# Revit family: vanity unit-hansgrohe-54195XXX-Xevolos E Vanity unit Slate Matt Grey 1180_550 with 2 drawers for consoles with countertop basin ground
name_source: partatom
category: Furniture
units: mm (PartAtom-declared; Revit-internal decimal feet)

## family parameters
Always vertical = Yes
Cut with Voids When Loaded = No
OmniClass Number = 23.40.00.00
OmniClass Title = Equipment and Furnishings
Room Calculation Point = No
Shared = Yes
Work Plane-Based = No

## types (6) — shared parameters
BASENUMBER = 54195
BIMOBJECT = Sanitary: Compound units
CATALOG = Hansgrohe
COLLECTION = vanity unit
COLLECTIONSET = Xevolos E
DESIGN = Germany
ETIM = EC011381 | Bathroom furniture set
IFC = Furnishing element
L = 1180
MASTERFORMAT = 12 35 30.23 | Bathroom Casework
Manufacturer = Hansgrohe
NAME = Xevolos E Vanity unit Slate Matt Grey 1180/550 with 2 drawers for consoles with countertop basin ground
NBSYN = $ARTNR.-$OBERFLAECHE.-$SURFACE.-$LODLEVEL.
NN = Vanity unit with 2 drawers for consoles with countertop basin ground
OBERFLAECHE = SLATE_MATT_GREY
OBJECTTYPE = Object (single object)
OMNICLASS = 23-21 19 15 33 13 | Residential Bathroom Specialty Casework
PERMALINK = 54195XXX
PRODUCTURL = https://pro.hansgrohe.com
REGION = Worldwide
UNICLASS2015 = Pr_40_30_78_05 | Bathroom furniture
UNICLASS_2015_CODE = 40_30_78_05
UNIFORMATII = E2010 | Fixed Furnishings
UNSPSC = 56 | Furniture and Furnishings
WEIGHT = 58.6
etim7_EC011381 = EC011381

## per-type parameters (varying)
| type | ARTNR | IDNR | LODLEVEL | SURFACE |
| 54195390-SLATE_MATT_GREY-PATTEREND_BRONZE-200 | 54195390 | 25 | 200 | PATTEREND_BRONZE |
| 54195390-SLATE_MATT_GREY-PATTEREND_BRONZE-400 | 54195390 | 25 | 400 | PATTEREND_BRONZE |
| 54195730-SLATE_MATT_GREY-DARK_OAK-200 | 54195730 | 26 | 200 | DARK_OAK |
| 54195730-SLATE_MATT_GREY-DARK_OAK-400 | 54195730 | 26 | 400 | DARK_OAK |
| 54195770-SLATE_MATT_GREY-METALLIC_SLATE_GREY-200 | 54195770 | 27 | 200 | METALLIC_SLATE_GREY |
| 54195770-SLATE_MATT_GREY-METALLIC_SLATE_GREY-400 | 54195770 | 27 | 400 | METALLIC_SLATE_GREY |

note: column(s) folded — value = type name in every type: LINA, Model, NB

type visibility flags: 6 boolean params named "<type name>_RX0RY0RZ0TX0TY0TZ0_V" — each type sets only its own to Yes (folded from table)

## geometry (parser evidence)
native form markers: Sweep x30
no freeform markers — native parametric forms only
